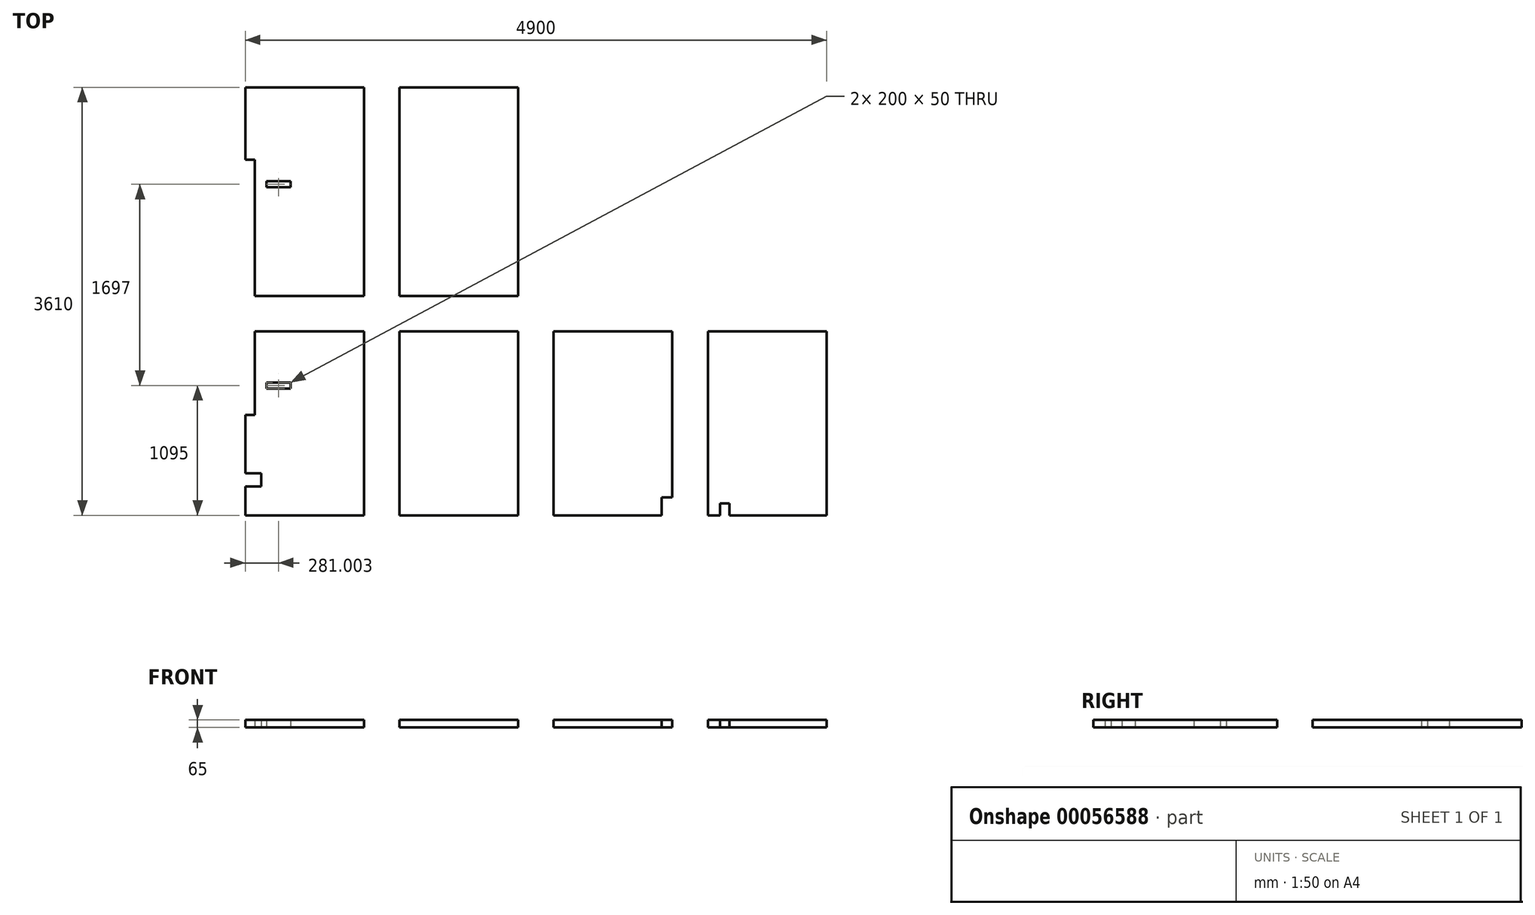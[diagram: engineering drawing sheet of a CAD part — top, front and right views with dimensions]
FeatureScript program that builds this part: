
annotation { "Feature Type Name" : "Feature", "Feature Type Description" : "" }
export const myFeature = defineFeature(function(context is Context, id is Id, definition is map)
    precondition{}
    {
        {
            var Q0;
            Q0=qCreatedBy(makeId("Top.planeOp"),FACE);
            var sketch = newSketch(context, id + "F0", { "sketchPlane" : qUnion([Q0])});
            skLineSegment(sketch, "E0.bottom", {"start": v(-679.89, 902.64) * mm, "end": v(320.11, 902.64) * mm});
            skLineSegment(sketch, "E0.top", {"start": v(-599.89, -857.36) * mm, "end": v(320.11, -857.36) * mm});
            skLineSegment(sketch, "E0.left", {"start": v(-679.89, 902.64) * mm, "end": v(-679.89, 292.64) * mm});
            skLineSegment(sketch, "E0.right", {"start": v(320.11, 902.64) * mm, "end": v(320.11, -857.36) * mm});
            skLineSegment(sketch, "E1.top", {"start": v(-679.89, 292.64) * mm, "end": v(-599.89, 292.64) * mm});
            skLineSegment(sketch, "E1.right", {"start": v(-599.89, -857.36) * mm, "end": v(-599.89, 292.64) * mm});
            skLineSegment(sketch, "E2.bottom", {"start": v(-498.89, 109.64) * mm, "end": v(-298.89, 109.64) * mm});
            skLineSegment(sketch, "E2.top", {"start": v(-498.89, 59.64) * mm, "end": v(-298.89, 59.64) * mm});
            skLineSegment(sketch, "E2.left", {"start": v(-498.89, 109.64) * mm, "end": v(-498.89, 59.64) * mm});
            skLineSegment(sketch, "E2.right", {"start": v(-298.89, 109.64) * mm, "end": v(-298.89, 59.64) * mm});
            skLineSegment(sketch, "E3.bottom", {"start": v(620.11, 902.64) * mm, "end": v(1620.11, 902.64) * mm});
            skLineSegment(sketch, "E3.top", {"start": v(620.11, -857.36) * mm, "end": v(1620.11, -857.36) * mm});
            skLineSegment(sketch, "E3.left", {"start": v(620.11, 902.64) * mm, "end": v(620.11, -857.36) * mm});
            skLineSegment(sketch, "E3.right", {"start": v(1620.11, 902.64) * mm, "end": v(1620.11, -857.36) * mm});
            skLineSegment(sketch, "E4.bottom", {"start": v(-599.89, -1157.36) * mm, "end": v(320.11, -1157.36) * mm});
            skLineSegment(sketch, "E4.top", {"start": v(-679.89, -2707.36) * mm, "end": v(320.11, -2707.36) * mm});
            skLineSegment(sketch, "E4.left", {"start": v(-679.89, -1859.36) * mm, "end": v(-679.89, -2354.36) * mm});
            skLineSegment(sketch, "E4.right", {"start": v(320.11, -1157.36) * mm, "end": v(320.11, -2707.36) * mm});
            skLineSegment(sketch, "E5.top", {"start": v(-679.89, -1859.36) * mm, "end": v(-599.89, -1859.36) * mm});
            skLineSegment(sketch, "E5.right", {"start": v(-599.89, -1157.36) * mm, "end": v(-599.89, -1859.36) * mm});
            skLineSegment(sketch, "E6.bottom", {"start": v(-679.89, -2354.36) * mm, "end": v(-544.89, -2354.36) * mm});
            skLineSegment(sketch, "E6.top", {"start": v(-679.89, -2464.36) * mm, "end": v(-544.89, -2464.36) * mm});
            skLineSegment(sketch, "E6.right", {"start": v(-544.89, -2354.36) * mm, "end": v(-544.89, -2464.36) * mm});
            skLineSegment(sketch, "E7.trimOffspring", {"start": v(-679.89, -2464.36) * mm, "end": v(-679.89, -2707.36) * mm});
            skLineSegment(sketch, "E8.bottom", {"start": v(-498.89, -1587.36) * mm, "end": v(-298.89, -1587.36) * mm});
            skLineSegment(sketch, "E8.top", {"start": v(-498.89, -1637.36) * mm, "end": v(-298.89, -1637.36) * mm});
            skLineSegment(sketch, "E8.left", {"start": v(-498.89, -1587.36) * mm, "end": v(-498.89, -1637.36) * mm});
            skLineSegment(sketch, "E8.right", {"start": v(-298.89, -1587.36) * mm, "end": v(-298.89, -1637.36) * mm});
            skLineSegment(sketch, "E9.bottom", {"start": v(620.11, -1157.36) * mm, "end": v(1620.11, -1157.36) * mm});
            skLineSegment(sketch, "E9.top", {"start": v(620.11, -2707.36) * mm, "end": v(1620.11, -2707.36) * mm});
            skLineSegment(sketch, "E9.left", {"start": v(620.11, -1157.36) * mm, "end": v(620.11, -2707.36) * mm});
            skLineSegment(sketch, "E9.right", {"start": v(1620.11, -1157.36) * mm, "end": v(1620.11, -2707.36) * mm});
            skLineSegment(sketch, "E10.bottom", {"start": v(1920.11, -1157.36) * mm, "end": v(2920.11, -1157.36) * mm});
            skLineSegment(sketch, "E10.top", {"start": v(1920.11, -2707.36) * mm, "end": v(2830.11, -2707.36) * mm});
            skLineSegment(sketch, "E10.left", {"start": v(1920.11, -1157.36) * mm, "end": v(1920.11, -2707.36) * mm});
            skLineSegment(sketch, "E10.right", {"start": v(2920.11, -1157.36) * mm, "end": v(2920.11, -2557.36) * mm});
            skLineSegment(sketch, "E11.top", {"start": v(2920.11, -2557.36) * mm, "end": v(2830.11, -2557.36) * mm});
            skLineSegment(sketch, "E11.right", {"start": v(2830.11, -2707.36) * mm, "end": v(2830.11, -2557.36) * mm});
            skLineSegment(sketch, "E12.bottom", {"start": v(3220.11, -1157.36) * mm, "end": v(4220.11, -1157.36) * mm});
            skLineSegment(sketch, "E12.top", {"start": v(3220.11, -2707.36) * mm, "end": v(3322.11, -2707.36) * mm});
            skLineSegment(sketch, "E12.left", {"start": v(3220.11, -1157.36) * mm, "end": v(3220.11, -2707.36) * mm});
            skLineSegment(sketch, "E12.right", {"start": v(4220.11, -1157.36) * mm, "end": v(4220.11, -2707.36) * mm});
            skLineSegment(sketch, "E13.top", {"start": v(3322.11, -2607.36) * mm, "end": v(3402.11, -2607.36) * mm});
            skLineSegment(sketch, "E13.left", {"start": v(3322.11, -2707.36) * mm, "end": v(3322.11, -2607.36) * mm});
            skLineSegment(sketch, "E13.right", {"start": v(3402.11, -2707.36) * mm, "end": v(3402.11, -2607.36) * mm});
            skLineSegment(sketch, "E14.trimOffspring", {"start": v(3402.11, -2707.36) * mm, "end": v(4220.11, -2707.36) * mm});
            skSolve(sketch);
        }
        {
            var Q0;
            Q0 = qSketchRegion(id + "F0", true);
            extrude(context, id + "F1", {"entities" : qUnion([Q0]), "depth" : 65 * mm});
        }
    });
